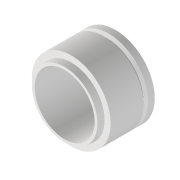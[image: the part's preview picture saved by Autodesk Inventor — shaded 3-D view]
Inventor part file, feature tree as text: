
AUTODESK INVENTOR PART (.ipt)
format: ipt  version: 2022 (Build 260153000, 153)  size: 122,368 bytes
history: native  units: mm
features: sketch x2, revolve x1, extrude x1
ambient origin geometry x8: Origin, YZ Plane, XZ Plane, XY Plane, X Axis, Y Axis, Z Axis, Center Point
bodies: Volumenkörper1 (feature_tree)
feature tree (4):
  revolve  "Umdrehung1"
  extrude  "Extrusion1"  Depth=2.0mm
  sketch  "Skizze1"  dims[d0=4.0mm d1=2.0mm]
  sketch  "Skizze2"  dims[d2=135.0deg d3=20.0mm d4=23.95mm d5=20.25mm d6=4.0mm d7=2.0mm d8=90.0deg d9=10.0mm d10=0.872665mm]
